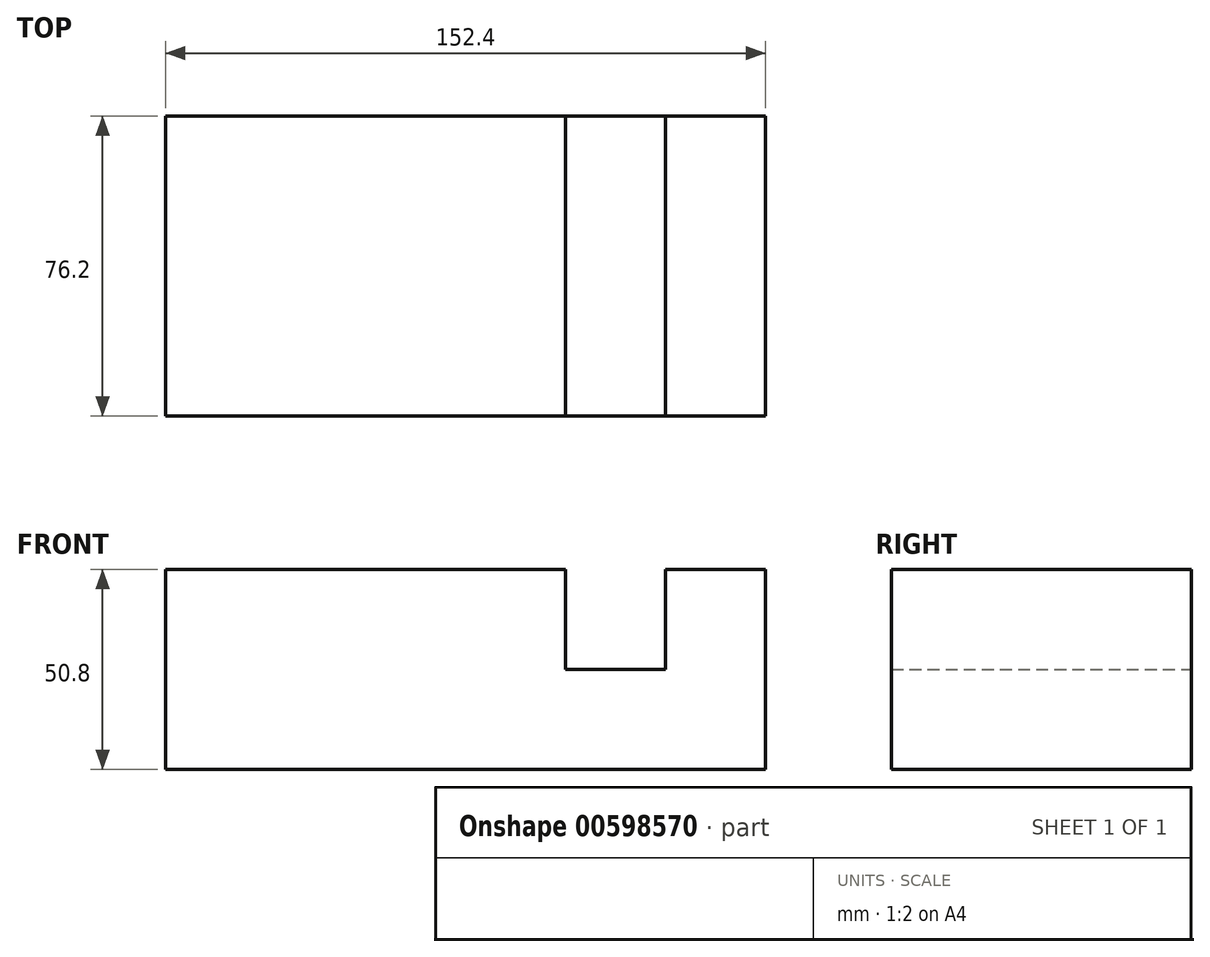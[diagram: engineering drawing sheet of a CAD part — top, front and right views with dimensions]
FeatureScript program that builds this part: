
annotation { "Feature Type Name" : "Feature", "Feature Type Description" : "" }
export const myFeature = defineFeature(function(context is Context, id is Id, definition is map)
    precondition{}
    {
        {
            var Q0;
            Q0=qCreatedBy(makeId("Front.planeOp"),FACE);
            var sketch = newSketch(context, id + "F0", { "sketchPlane" : qUnion([Q0])});
            skLineSegment(sketch, "E0", {"start": v(0, 0) * mm, "end": v(0, 50.8) * mm});
            skLineSegment(sketch, "E1", {"start": v(0, 50.8) * mm, "end": v(101.6, 50.8) * mm});
            skLineSegment(sketch, "E2", {"start": v(101.6, 50.8) * mm, "end": v(101.6, 25.4) * mm});
            skLineSegment(sketch, "E3", {"start": v(101.6, 25.4) * mm, "end": v(127, 25.4) * mm});
            skLineSegment(sketch, "E4", {"start": v(127, 25.4) * mm, "end": v(127, 50.8) * mm});
            skLineSegment(sketch, "E5", {"start": v(127, 50.8) * mm, "end": v(152.4, 50.8) * mm});
            skLineSegment(sketch, "E6", {"start": v(152.4, 50.8) * mm, "end": v(152.4, 0) * mm});
            skLineSegment(sketch, "E7", {"start": v(152.4, 0) * mm, "end": v(0, 0) * mm});
            skSolve(sketch);
        }
        {
            var Q0;
            Q0=qSketchRegion(id+"F0",true);
            extrude(context, id + "F1", {"entities" : qUnion([Q0]), "depth" : 76.2 * mm, "offsetDistance" : 25.4 * mm});
        }
    });
